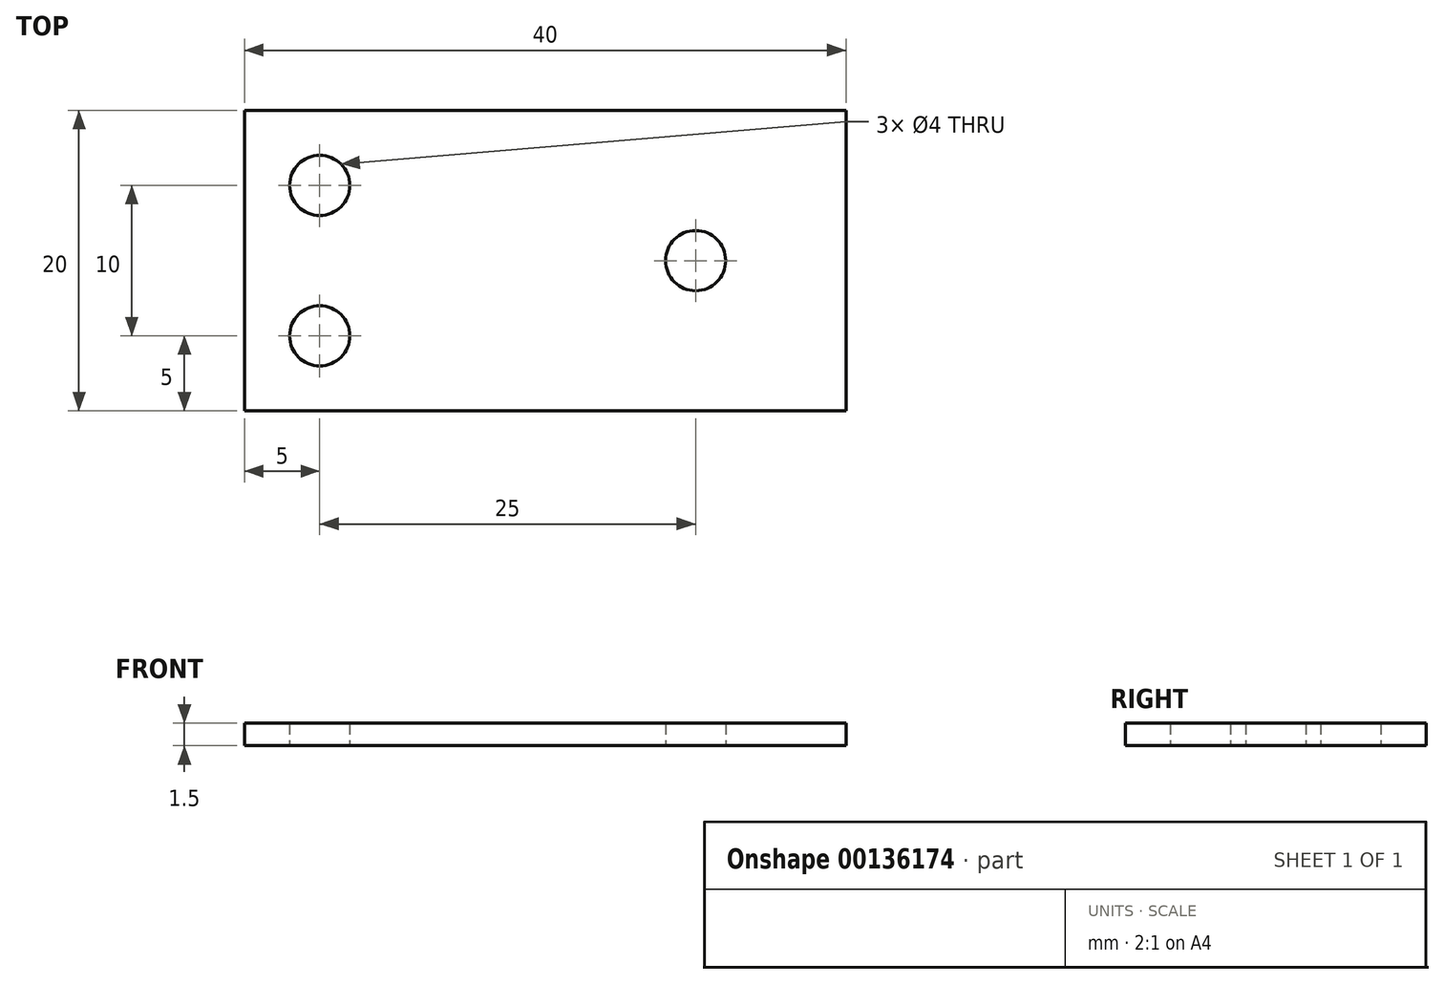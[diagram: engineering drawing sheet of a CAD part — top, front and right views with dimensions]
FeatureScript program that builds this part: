
annotation { "Feature Type Name" : "Feature", "Feature Type Description" : "" }
export const myFeature = defineFeature(function(context is Context, id is Id, definition is map)
    precondition{}
    {
        {
            var Q0;
            Q0=qCreatedBy(makeId("Top.planeOp"),FACE);
            var sketch = newSketch(context, id + "F0", { "sketchPlane" : qUnion([Q0])});
            skLineSegment(sketch, "E0.bottom", {"start": v(0, 0) * mm, "end": v(40, 0) * mm});
            skLineSegment(sketch, "E0.top", {"start": v(0, -20) * mm, "end": v(40, -20) * mm});
            skLineSegment(sketch, "E0.left", {"start": v(0, 0) * mm, "end": v(0, -20) * mm});
            skLineSegment(sketch, "E0.right", {"start": v(40, 0) * mm, "end": v(40, -20) * mm});
            skCircle(sketch, "E1", {"center": v(5, -5) * mm, "radius": 2 * mm});
            skCircle(sketch, "E2", {"center": v(5, -15) * mm, "radius": 2 * mm});
            skCircle(sketch, "E3", {"center": v(30, -10) * mm, "radius": 2 * mm});
            skSolve(sketch);
        }
        {
            var Q0;
            Q0 = qSketchRegion(id + "F0", true);
            extrude(context, id + "F1", {"entities" : qUnion([Q0]), "depth" : 1.5 * mm});
        }
    });
